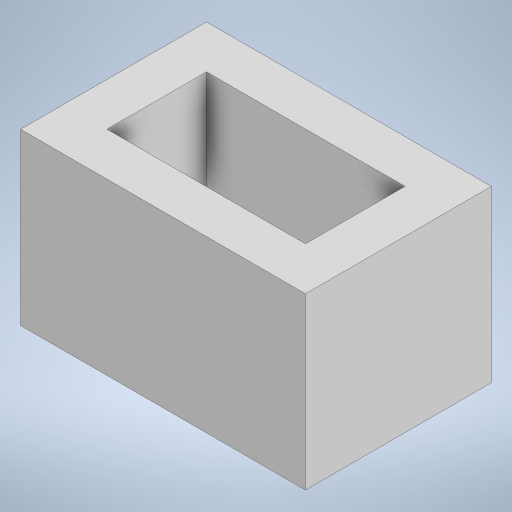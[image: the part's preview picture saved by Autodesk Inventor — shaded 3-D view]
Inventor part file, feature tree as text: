
AUTODESK INVENTOR PART (.ipt)
format: ipt  version: 2023.5 (Build 275446000, 446)  size: 191,488 bytes
history: native  units: in
note: dims shown in document units (in); Inventor stores cm internally (conversion verified against a paired STEP export)
features: extrude x3, sketch x3
ambient origin geometry x8: Origin, YZ Plane, XZ Plane, XY Plane, X Axis, Y Axis, Z Axis, Center Point
bodies: Solid1 (feature_tree)
feature tree (6):
  extrude  "Extrusion1"  Depth=0.2717in
  extrude  "Extrusion2"  Depth=0.1181in
  extrude  "Extrusion3"  Depth=0.1181in
  sketch  "Sketch1"  dims[d0=0.5421in d1=0.2717in]
  sketch  "Sketch2"  dims[d2=0.1181in d3=0.1181in]
  sketch  "Sketch3"  dims[d4=0.1181in d5=0.1181in d6=0.3465in d7=0.0in d8=0.1181in d9=0.0in d10=0.3268in d11=0.1181in d12=0.0in]
